# Revit family: LBE_Precast-Console Beam_Spæncom
name_source: partatom
category: Structural Framing
revit_build: Autodesk Revit 2014 (Build: 20130308_1515(x64)
units: mm (PartAtom-declared; Revit-internal decimal feet)

## types (8) — shared parameters
Console thickness = 80 mm  [stored 0.262467 ft]
Console width = 120 mm  [stored 0.393701 ft]
Height (bjælkekroppen) = 140 mm  [stored 0.459318 ft]
Manufacturer = Spæncom

## per-type parameters (varying)
| type | Height element | Model | Width beam top | Width element |
| LBE 50/22 | 300 mm | LBE 50/22 | 355 mm | 500 mm  [stored 1.64042 ft] |
| LBE 50/27 | 350 mm  [stored 1.14829 ft] | LBE 50/27 | 340 mm  [stored 1.11549 ft] | 500 mm  [stored 1.64042 ft] |
| LBE 50/32 | 400 mm  [stored 1.31234 ft] | LBE 50/32 | 325 mm  [stored 1.06627 ft] | 500 mm  [stored 1.64042 ft] |
| LBE 50/40 | 480 mm  [stored 1.5748 ft] | LBE 50/40 | 300 mm | 500 mm  [stored 1.64042 ft] |
| LBE 66/22 | 300 mm | LBE 66/22 | 515 mm  [stored 1.68963 ft] | 660 mm |
| LBE 66(27 | 350 mm  [stored 1.14829 ft] | LBE 66/27 | 500 mm  [stored 1.64042 ft] | 660 mm |
| LBE 66/32 | 400 mm  [stored 1.31234 ft] | LBE 66/32 | 485 mm  [stored 1.59121 ft] | 660 mm |
| LBE 66/40 | 480 mm  [stored 1.5748 ft] | LBE 66/40 | 460 mm  [stored 1.50919 ft] | 660 mm |

note: [stored X ft] marks values corroborated as IEEE doubles in the binary element streams (Revit-internal decimal feet)

## geometry (parser evidence)
native form markers: Sweep x1
no freeform markers — native parametric forms only
